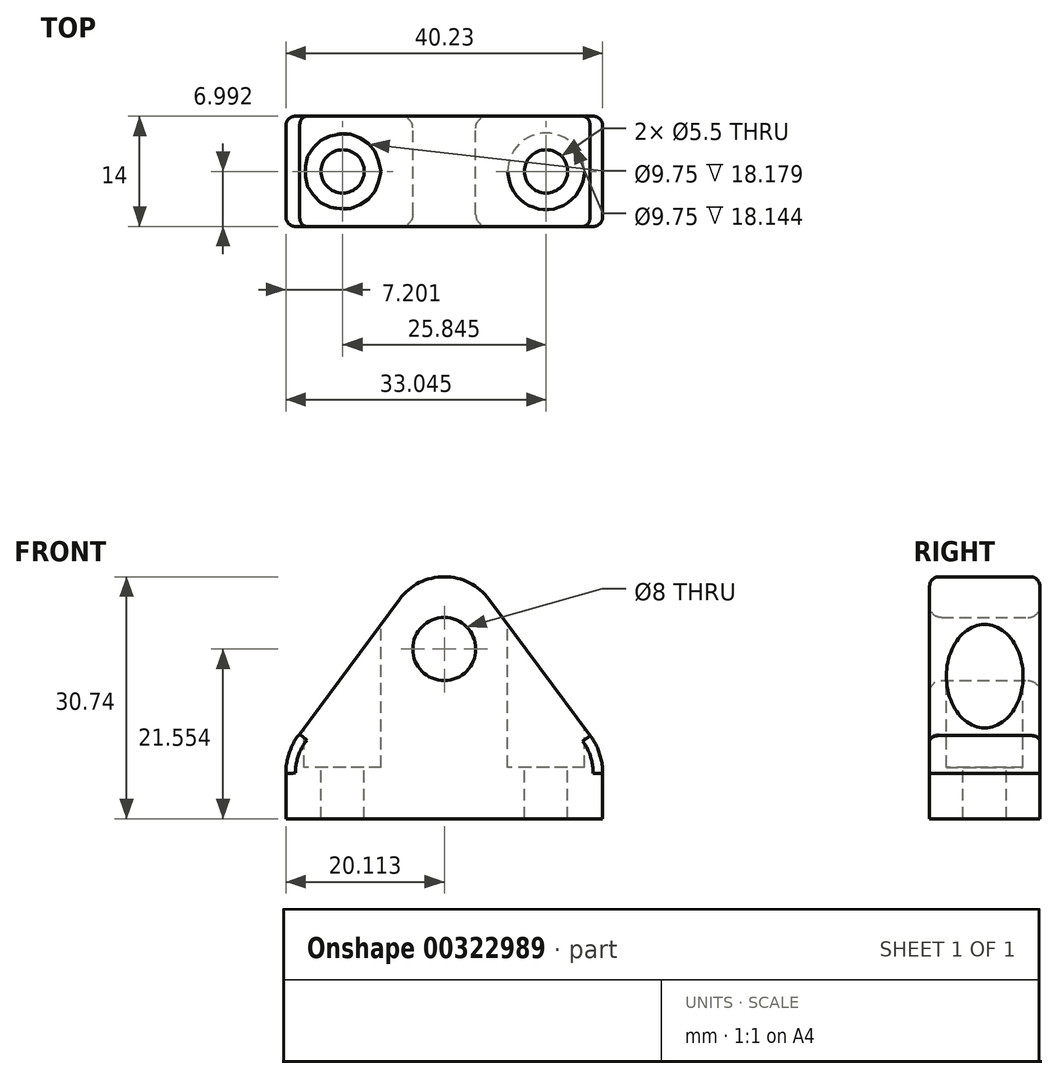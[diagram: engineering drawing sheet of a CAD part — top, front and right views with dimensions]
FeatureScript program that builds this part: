
annotation { "Feature Type Name" : "Feature", "Feature Type Description" : "" }
export const myFeature = defineFeature(function(context is Context, id is Id, definition is map)
    precondition{}
    {
        {
            var Q0;
            Q0=qCreatedBy(makeId("Top.planeOp"),FACE);
            cPlane(context, id + "F0", {"entities" : qUnion([Q0]), "cplaneType" : CPlaneType.OFFSET, "offset" : 10 * mm, "width" : 150 * mm, "height" : 150 * mm});
        }
        {
            var Q0;
            Q0=qCreatedBy(makeId("Front.planeOp"),FACE);
            var sketch = newSketch(context, id + "F1", { "sketchPlane" : qUnion([Q0])});
            skLineSegment(sketch, "E0.bottom", {"start": v(-40.51, -15.12) * mm, "end": v(-0.3, -15.12) * mm});
            skLineSegment(sketch, "E0.left", {"start": v(-40.51, -15.12) * mm, "end": v(-40.51, -9.35) * mm});
            skLineSegment(sketch, "E0.right", {"start": v(-0.3, -15.12) * mm, "end": v(-0.3, -9.35) * mm});
            skLineSegment(sketch, "E1", {"start": v(-38.78, -4.4) * mm, "end": v(-26.1, 12.75) * mm});
            skLineSegment(sketch, "E2", {"start": v(-14.7, 12.73) * mm, "end": v(-1.88, -4.56) * mm});
            skFitSpline(sketch, "E3", {"points": [v(-40.51, -9.35) * mm, v(-38.78, -4.4) * mm], "startDerivative": vector(-0.16, 4.57) * mm, "endDerivative": vector(3.41, 3.78) * mm});
            skFitSpline(sketch, "E4", {"points": [v(-0.3, -9.35) * mm, v(-1.88, -4.56) * mm], "startDerivative": vector(0.07, 5.39) * mm, "endDerivative": vector(-2.69, 3.36) * mm});
            skPoint(sketch, "E5", {"position": v(-20.4, 6.43) * mm});
            skCircle(sketch, "E6", {"center": v(-20.4, 6.43) * mm, "radius": 4 * mm});
            skArc(sketch, "E7", {"start": v(-26.1, 12.75) * mm, "mid": v(-20.39, 15.62) * mm, "end": v(-14.7, 12.73) * mm});
            skSolve(sketch);
        }
        {
            var Q0;
            Q0 = qSketchRegion(id + "F1", true);
            extrude(context, id + "F2", {"entities" : qUnion([Q0]), "endBound" : BoundingType.SYMMETRIC, "depth" : 14 * mm});
        }
        {
            var Q0;
            Q0=qCreatedBy(id+"F0.planeOp",FACE);
            var sketch = newSketch(context, id + "F3", { "sketchPlane" : qUnion([Q0])});
            skLineSegment(sketch, "E8.bottom", {"start": v(-40.51, 7) * mm, "end": v(-0.29, 7) * mm});
            skLineSegment(sketch, "E8.top", {"start": v(-40.51, -7.01) * mm, "end": v(-0.29, -7.01) * mm});
            skLineSegment(sketch, "E8.left", {"start": v(-40.51, 7) * mm, "end": v(-40.51, -7.01) * mm});
            skLineSegment(sketch, "E8.right", {"start": v(-0.29, 7) * mm, "end": v(-0.29, -7.01) * mm});
            skLineSegment(sketch, "E9", {"start": v(-26.13, 7) * mm, "end": v(-40.51, -7.01) * mm, "construction": true});
            skLineSegment(sketch, "E10", {"start": v(-0.29, 7) * mm, "end": v(-14.66, -7.01) * mm, "construction": true});
            skPoint(sketch, "E11.positionSnap0", {"position": v(-7.47, 0) * mm});
            skPoint(sketch, "E12.positionSnap0", {"position": v(-33.32, 0) * mm});
            skSolve(sketch);
        }
        {
            var Q0;
            Q0=sQuery(id+"F3.wireOp",VERTEX,"E12.positionSnap0");
            var Q1;
            Q1=sQuery(id+"F3.wireOp",VERTEX,"E11.positionSnap0");
            var Q2;
            Q2=makeQuery(id+"F2.opExtrude","SWEPT_BODY",BODY,{"disambiguationData":[OSD([sQuery(id+"F1.wireOp",EDGE,"E0.bottom"),sQuery(id+"F1.wireOp",EDGE,"E0.left"),sQuery(id+"F1.wireOp",EDGE,"E0.right"),sQuery(id+"F1.wireOp",EDGE,"E1"),sQuery(id+"F1.wireOp",EDGE,"E2"),sQuery(id+"F1.wireOp",EDGE,"E3"),sQuery(id+"F1.wireOp",EDGE,"E4"),sQuery(id+"F1.wireOp",EDGE,"E6"),sQuery(id+"F1.wireOp",EDGE,"E7")])]});
            hole(context, id + "F4", {"style" : HoleStyle.C_BORE, "endStyle" : HoleEndStyle.BLIND, "standardTappedOrClearance" : lookupTablePath({ "standard" : "ISO", "fit" : "Normal", "size" : "M5", "type" : "Clearance" }), "standardBlindInLast" : lookupTablePath({ "fit" : "Standard", "standard" : "ISO", "size" : "M5", "type" : "Clearance" }), "holeDiameter" : 5.5 * mm, "cBoreDiameter" : 9.75 * mm, "cBoreDepth" : 5 * mm, "holeDepth" : 20 * mm, "tappedDepth" : 12 * mm, "tapClearance" : 3, "locations" : qUnion([Q0, Q1]), "scope" : qUnion([Q2])});
        }
        {
            var Q0;
            Q0=makeQuery(id+"F2.opExtrude","CAP_EDGE",EDGE,{"disambiguationData":[OSD([sQuery(id+"F1.wireOp",EDGE,"E0.right")])],"isStart":true});
            var Q1;
            Q1=makeQuery(id+"F2.opExtrude","CAP_EDGE",EDGE,{"disambiguationData":[OSD([sQuery(id+"F1.wireOp",EDGE,"E4")])],"isStart":true});
            var Q2;
            Q2=makeQuery(id+"F2.opExtrude","CAP_EDGE",EDGE,{"disambiguationData":[OSD([sQuery(id+"F1.wireOp",EDGE,"E2")])],"isStart":true});
            var Q3;
            Q3=makeQuery(id+"F2.opExtrude","CAP_EDGE",EDGE,{"disambiguationData":[OSD([sQuery(id+"F1.wireOp",EDGE,"E7")])],"isStart":true});
            var Q4;
            Q4=makeQuery(id+"F2.opExtrude","CAP_EDGE",EDGE,{"disambiguationData":[OSD([sQuery(id+"F1.wireOp",EDGE,"E1")])],"isStart":true});
            var Q5;
            Q5=makeQuery(id+"F2.opExtrude","CAP_EDGE",EDGE,{"disambiguationData":[OSD([sQuery(id+"F1.wireOp",EDGE,"E3")])],"isStart":true});
            var Q6;
            Q6=makeQuery(id+"F2.opExtrude","CAP_EDGE",EDGE,{"disambiguationData":[OSD([sQuery(id+"F1.wireOp",EDGE,"E0.left")])],"isStart":true});
            var Q7;
            Q7=makeQuery(id+"F2.opExtrude","CAP_EDGE",EDGE,{"disambiguationData":[OSD([sQuery(id+"F1.wireOp",EDGE,"E0.left")])],"isStart":false});
            var Q8;
            Q8=makeQuery(id+"F2.opExtrude","CAP_EDGE",EDGE,{"disambiguationData":[OSD([sQuery(id+"F1.wireOp",EDGE,"E3")])],"isStart":false});
            var Q9;
            Q9=makeQuery(id+"F2.opExtrude","CAP_EDGE",EDGE,{"disambiguationData":[OSD([sQuery(id+"F1.wireOp",EDGE,"E1")])],"isStart":false});
            var Q10;
            Q10=makeQuery(id+"F2.opExtrude","CAP_EDGE",EDGE,{"disambiguationData":[OSD([sQuery(id+"F1.wireOp",EDGE,"E7")])],"isStart":false});
            var Q11;
            Q11=makeQuery(id+"F2.opExtrude","CAP_EDGE",EDGE,{"disambiguationData":[OSD([sQuery(id+"F1.wireOp",EDGE,"E2")])],"isStart":false});
            var Q12;
            Q12=makeQuery(id+"F2.opExtrude","CAP_EDGE",EDGE,{"disambiguationData":[OSD([sQuery(id+"F1.wireOp",EDGE,"E4")])],"isStart":false});
            var Q13;
            Q13=makeQuery(id+"F2.opExtrude","CAP_EDGE",EDGE,{"disambiguationData":[OSD([sQuery(id+"F1.wireOp",EDGE,"E0.right")])],"isStart":false});
            fillet(context, id + "F5", {"entities" : qUnion([Q0, Q1, Q2, Q3, Q4, Q5, Q6, Q7, Q8, Q9, Q10, Q11, Q12, Q13]), "radius" : 1.2 * mm, "allowEdgeOverflow" : false});
        }
        {
            var Q0;
            Q0=makeQuery(id+"F2.opExtrude","CAP_EDGE",EDGE,{"disambiguationData":[OSD([sQuery(id+"F1.wireOp",EDGE,"E6")])],"isStart":false});
            var Q1;
            Q1=makeQuery(id+"F2.opExtrude","CAP_EDGE",EDGE,{"disambiguationData":[OSD([sQuery(id+"F1.wireOp",EDGE,"E6")])],"isStart":true});
            fillet(context, id + "F6", {"entities" : qUnion([Q0, Q1]), "radius" : 1.5 * mm, "tangentPropagation" : true, "allowEdgeOverflow" : false});
        }
    });
